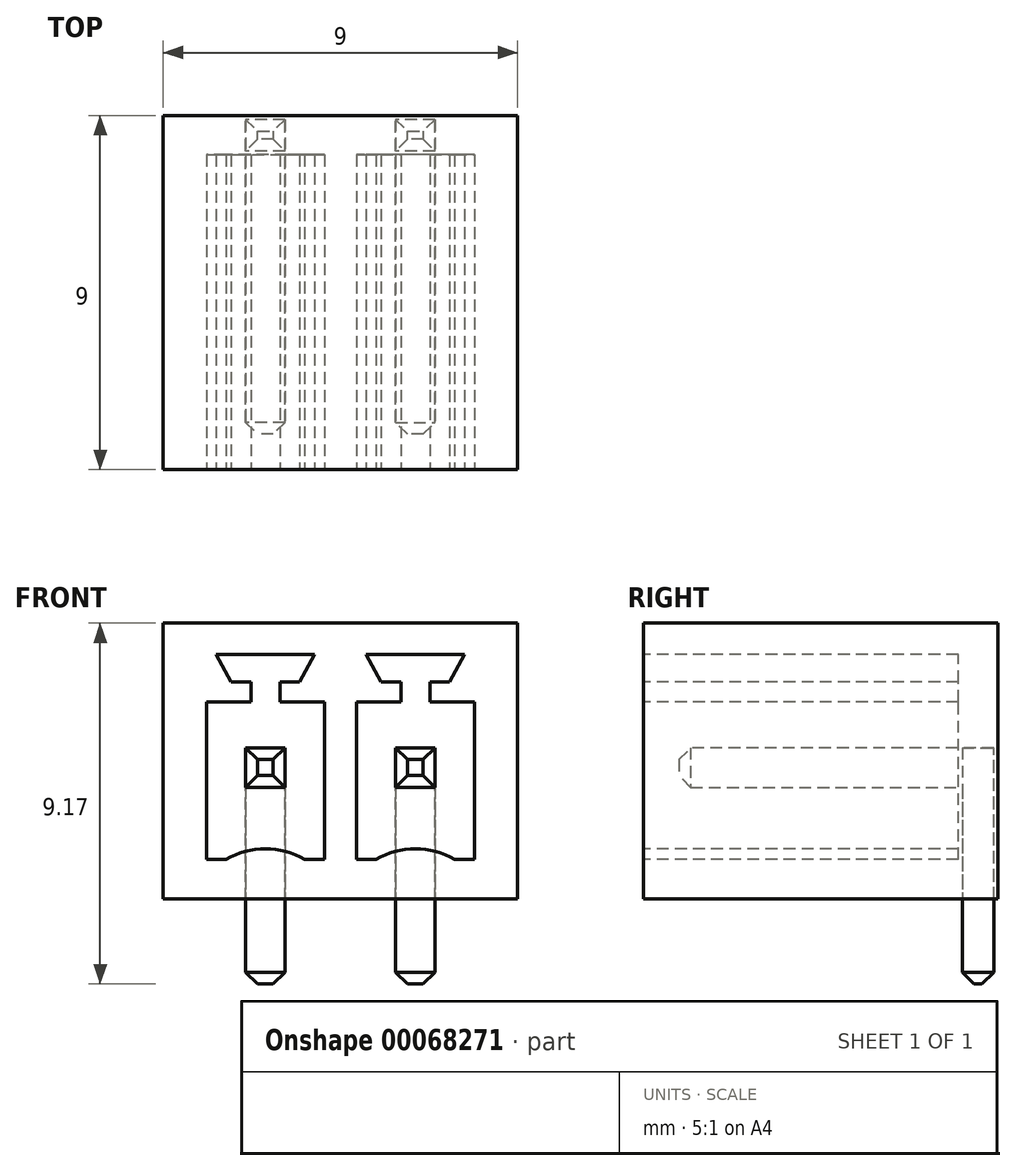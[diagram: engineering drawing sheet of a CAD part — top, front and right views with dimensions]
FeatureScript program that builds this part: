
annotation { "Feature Type Name" : "Feature", "Feature Type Description" : "" }
export const myFeature = defineFeature(function(context is Context, id is Id, definition is map)
    precondition{}
    {
        {
            var Q0;
            Q0=qCreatedBy(makeId("Top.planeOp"),FACE);
            var sketch = newSketch(context, id + "F0", { "sketchPlane" : qUnion([Q0])});
            skLineSegment(sketch, "E0.bottom", {"start": v(4.5, 4.5) * mm, "end": v(-4.5, 4.5) * mm});
            skLineSegment(sketch, "E0.top", {"start": v(4.5, -4.5) * mm, "end": v(-4.5, -4.5) * mm});
            skLineSegment(sketch, "E0.left", {"start": v(4.5, 4.5) * mm, "end": v(4.5, -4.5) * mm});
            skLineSegment(sketch, "E0.right", {"start": v(-4.5, 4.5) * mm, "end": v(-4.5, -4.5) * mm});
            skPoint(sketch, "E0.middle", {"position": v(0, 0) * mm});
            skSolve(sketch);
        }
        {
            var Q0;
            Q0=qSketchRegion(id+"F0",true);
            extrude(context, id + "F1", {"entities" : qUnion([Q0]), "depth" : 7 * mm});
        }
        {
            var Q0;
            Q0=makeQuery(id+"F1.opExtrude","SWEPT_FACE",FACE,{"disambiguationData":[OSD([sQuery(id+"F0.wireOp",EDGE,"E0.top")])]});
            var sketch = newSketch(context, id + "F2", { "sketchPlane" : qUnion([Q0])});
            skLineSegment(sketch, "E1", {"start": v(0, 0) * mm, "end": v(0, 7) * mm, "construction": true});
            skLineSegment(sketch, "E2", {"start": v(-0.4, 1) * mm, "end": v(-3.4, 1) * mm});
            skLineSegment(sketch, "E3", {"start": v(-3.4, 1) * mm, "end": v(-3.4, 5) * mm});
            skLineSegment(sketch, "E4", {"start": v(-3.4, 5) * mm, "end": v(-2.27, 5) * mm});
            skLineSegment(sketch, "E5", {"start": v(-2.27, 5) * mm, "end": v(-2.27, 5.5) * mm});
            skLineSegment(sketch, "E6", {"start": v(-2.27, 5.5) * mm, "end": v(-2.77, 5.5) * mm});
            skLineSegment(sketch, "E7", {"start": v(-2.77, 5.5) * mm, "end": v(-3.15, 6.2) * mm});
            skLineSegment(sketch, "E8", {"start": v(-3.15, 6.2) * mm, "end": v(-0.65, 6.2) * mm});
            skLineSegment(sketch, "E9", {"start": v(-0.66, 6.2) * mm, "end": v(-1.04, 5.5) * mm});
            skLineSegment(sketch, "E10", {"start": v(-1.04, 5.5) * mm, "end": v(-1.54, 5.5) * mm});
            skLineSegment(sketch, "E11", {"start": v(-1.54, 5.5) * mm, "end": v(-1.54, 5) * mm});
            skLineSegment(sketch, "E12", {"start": v(-1.54, 5) * mm, "end": v(-0.4, 5) * mm});
            skLineSegment(sketch, "E13", {"start": v(-0.4, 5) * mm, "end": v(-0.4, 1) * mm});
            skLineSegment(sketch, "E14", {"start": v(-1.9, 1) * mm, "end": v(-1.9, 6.2) * mm, "construction": true});
            skLineSegment(sketch, "E15.MirrorCS", {"start": v(0.66, 6.2) * mm, "end": v(1.04, 5.5) * mm});
            skLineSegment(sketch, "E16.MirrorCS", {"start": v(1.04, 5.5) * mm, "end": v(1.54, 5.5) * mm});
            skLineSegment(sketch, "E17.MirrorCS", {"start": v(1.54, 5.5) * mm, "end": v(1.54, 5) * mm});
            skLineSegment(sketch, "E18.MirrorCS", {"start": v(1.54, 5) * mm, "end": v(0.4, 5) * mm});
            skLineSegment(sketch, "E19.MirrorCS", {"start": v(2.27, 5) * mm, "end": v(2.27, 5.5) * mm});
            skLineSegment(sketch, "E20.MirrorCS", {"start": v(0.4, 5) * mm, "end": v(0.4, 1) * mm});
            skLineSegment(sketch, "E21.MirrorCS", {"start": v(3.4, 5) * mm, "end": v(2.27, 5) * mm});
            skLineSegment(sketch, "E22.MirrorCS", {"start": v(3.4, 1) * mm, "end": v(3.4, 5) * mm});
            skLineSegment(sketch, "E23.MirrorCS", {"start": v(0.4, 1) * mm, "end": v(3.4, 1) * mm});
            skLineSegment(sketch, "E24.MirrorCS", {"start": v(3.15, 6.2) * mm, "end": v(0.65, 6.2) * mm});
            skLineSegment(sketch, "E25.MirrorCS", {"start": v(2.27, 5.5) * mm, "end": v(2.77, 5.5) * mm});
            skLineSegment(sketch, "E26.MirrorCS", {"start": v(2.77, 5.5) * mm, "end": v(3.15, 6.2) * mm});
            skSolve(sketch);
        }
        {
            var Q0;
            Q0=qSketchRegion(id+"F2",true);
            extrude(context, id + "F3", {"entities" : qUnion([Q0]), "operationType" : NewBodyOperationType.REMOVE, "oppositeDirection" : true, "depth" : 8 * mm});
        }
        {
            var Q0;
            Q0=makeQuery(id+"F1.opExtrude","SWEPT_FACE",FACE,{"disambiguationData":[OSD([sQuery(id+"F0.wireOp",EDGE,"E0.bottom")])]});
            var sketch = newSketch(context, id + "F4", { "sketchPlane" : qUnion([Q0])});
            skLineSegment(sketch, "E27.bottom", {"start": v(-2.4, 3.84) * mm, "end": v(-1.4, 3.84) * mm});
            skLineSegment(sketch, "E27.top", {"start": v(-2.4, 0) * mm, "end": v(-1.4, 0) * mm});
            skLineSegment(sketch, "E27.left", {"start": v(-2.4, 3.84) * mm, "end": v(-2.4, 0) * mm});
            skLineSegment(sketch, "E27.right", {"start": v(-1.4, 3.84) * mm, "end": v(-1.4, 0) * mm});
            skLineSegment(sketch, "E28.bottom", {"start": v(1.4, 3.84) * mm, "end": v(2.4, 3.84) * mm});
            skLineSegment(sketch, "E28.top", {"start": v(1.4, 0) * mm, "end": v(2.4, 0) * mm});
            skLineSegment(sketch, "E28.left", {"start": v(1.4, 3.84) * mm, "end": v(1.4, 0) * mm});
            skLineSegment(sketch, "E28.right", {"start": v(2.4, 3.84) * mm, "end": v(2.4, 0) * mm});
            skPoint(sketch, "E29.centerSnap0", {"position": v(-1.9, 3.84) * mm});
            skPoint(sketch, "E30.centerSnap0", {"position": v(1.9, 3.84) * mm});
            skSolve(sketch);
        }
        {
            var Q0;
            {var subQ0=sQuery(id+"F4.wireOp",EDGE,"E27.top");Q0=makeQuery(id+"F4.imprint","IMPRINT",FACE,{"disambiguationData":[TD([[makeQuery(id+"F4.imprint","IMPRINT",EDGE,{"derivedFrom":subQ0}),1.0]])]});}
            var Q1;
            {var subQ0=sQuery(id+"F4.wireOp",EDGE,"E29");var subQ1=makeQuery(id+"F4.imprint","INTERSECT",VERTEX,{"derivedFrom":[sQuery(id+"F4.wireOp",EDGE,"E27.bottom"),subQ0]});Q1=makeQuery(id+"F4.imprint","IMPRINT",FACE,{"disambiguationData":[TD([[makeQuery(id+"F4.imprint","IMPRINT",EDGE,{"disambiguationData":[TD([[subQ1,1.0]])],"derivedFrom":subQ0}),1.0]])]});}
            var Q2;
            {var subQ0=sQuery(id+"F4.wireOp",EDGE,"E27.left");var subQ1=sQuery(id+"F4.wireOp",EDGE,"E27.bottom");var subQ2=makeQuery(id+"F4.imprint","INTERSECT",VERTEX,{"derivedFrom":[subQ1,subQ0]});Q2=makeQuery(id+"F4.imprint","IMPRINT",FACE,{"disambiguationData":[TD([[makeQuery(id+"F4.imprint","IMPRINT",EDGE,{"disambiguationData":[TD([[subQ2,-1.0]])],"derivedFrom":subQ1}),-1.0]])]});}
            var Q3;
            {var subQ0=sQuery(id+"F4.wireOp",EDGE,"E27.right");var subQ1=sQuery(id+"F4.wireOp",EDGE,"E27.bottom");var subQ2=makeQuery(id+"F4.imprint","INTERSECT",VERTEX,{"derivedFrom":[subQ1,subQ0]});Q3=makeQuery(id+"F4.imprint","IMPRINT",FACE,{"disambiguationData":[TD([[makeQuery(id+"F4.imprint","IMPRINT",EDGE,{"disambiguationData":[TD([[subQ2,1.0]])],"derivedFrom":subQ1}),-1.0]])]});}
            var Q4;
            {var subQ0=sQuery(id+"F4.wireOp",EDGE,"E28.top");Q4=makeQuery(id+"F4.imprint","IMPRINT",FACE,{"disambiguationData":[TD([[makeQuery(id+"F4.imprint","IMPRINT",EDGE,{"derivedFrom":subQ0}),1.0]])]});}
            var Q5;
            {var subQ0=sQuery(id+"F4.wireOp",EDGE,"E30");var subQ1=makeQuery(id+"F4.imprint","INTERSECT",VERTEX,{"derivedFrom":[sQuery(id+"F4.wireOp",EDGE,"E28.bottom"),subQ0]});Q5=makeQuery(id+"F4.imprint","IMPRINT",FACE,{"disambiguationData":[TD([[makeQuery(id+"F4.imprint","IMPRINT",EDGE,{"disambiguationData":[TD([[subQ1,1.0]])],"derivedFrom":subQ0}),1.0]])]});}
            var Q6;
            {var subQ0=sQuery(id+"F4.wireOp",EDGE,"E28.left");var subQ1=sQuery(id+"F4.wireOp",EDGE,"E28.bottom");var subQ2=makeQuery(id+"F4.imprint","INTERSECT",VERTEX,{"derivedFrom":[subQ1,subQ0]});Q6=makeQuery(id+"F4.imprint","IMPRINT",FACE,{"disambiguationData":[TD([[makeQuery(id+"F4.imprint","IMPRINT",EDGE,{"disambiguationData":[TD([[subQ2,-1.0]])],"derivedFrom":subQ1}),-1.0]])]});}
            var Q7;
            {var subQ0=sQuery(id+"F4.wireOp",EDGE,"E28.right");var subQ1=sQuery(id+"F4.wireOp",EDGE,"E28.bottom");var subQ2=makeQuery(id+"F4.imprint","INTERSECT",VERTEX,{"derivedFrom":[subQ1,subQ0]});Q7=makeQuery(id+"F4.imprint","IMPRINT",FACE,{"disambiguationData":[TD([[makeQuery(id+"F4.imprint","IMPRINT",EDGE,{"disambiguationData":[TD([[subQ2,1.0]])],"derivedFrom":subQ1}),-1.0]])]});}
            extrude(context, id + "F5", {"entities" : qUnion([Q0, Q1, Q2, Q3, Q4, Q5, Q6, Q7]), "operationType" : NewBodyOperationType.REMOVE, "oppositeDirection" : true, "depth" : 0.9 * mm});
        }
        {
            var Q0;
            Q0=qCreatedBy(makeId("Right.planeOp"),FACE);
            var sketch = newSketch(context, id + "F6", { "sketchPlane" : qUnion([Q0])});
            skLineSegment(sketch, "E31", {"start": v(4.4, -2.17) * mm, "end": v(4.4, 3.83) * mm});
            skLineSegment(sketch, "E32", {"start": v(4.4, 3.83) * mm, "end": v(-3.6, 3.83) * mm});
            skLineSegment(sketch, "E33", {"start": v(-3.6, 3.83) * mm, "end": v(-3.6, 2.83) * mm});
            skLineSegment(sketch, "E34", {"start": v(-3.6, 2.83) * mm, "end": v(3.6, 2.83) * mm});
            skLineSegment(sketch, "E35", {"start": v(3.6, 2.83) * mm, "end": v(3.6, -2.17) * mm});
            skLineSegment(sketch, "E36", {"start": v(3.6, -2.17) * mm, "end": v(4.4, -2.17) * mm});
            skSolve(sketch);
        }
        {
            var Q0;
            Q0=makeQuery(id+"F5.boolean.opBoolean","COPY",FACE,{"derivedFrom":makeQuery(id+"F5.opExtrude","SWEPT_FACE",FACE,{"disambiguationData":[OSD([sQuery(id+"F4.wireOp",EDGE,"E28.right")])]})});
            var sketch = newSketch(context, id + "F7", { "sketchPlane" : qUnion([Q0])});
            skLineSegment(sketch, "E37.0", {"start": v(-3.6, 3.83) * mm, "end": v(-3.6, 2.83) * mm});
            skLineSegment(sketch, "E38.0", {"start": v(4.4, 3.83) * mm, "end": v(-3.6, 3.83) * mm});
            skLineSegment(sketch, "E39.0", {"start": v(4.4, -2.17) * mm, "end": v(4.4, 3.83) * mm});
            skLineSegment(sketch, "E40.0", {"start": v(3.6, -2.17) * mm, "end": v(4.4, -2.17) * mm});
            skLineSegment(sketch, "E41.0", {"start": v(3.6, 2.83) * mm, "end": v(3.6, -2.17) * mm});
            skLineSegment(sketch, "E42.0", {"start": v(-3.6, 2.83) * mm, "end": v(3.6, 2.83) * mm});
            skSolve(sketch);
        }
        {
            var Q0;
            Q0=qSketchRegion(id+"F7",true);
            extrude(context, id + "F8", {"entities" : qUnion([Q0]), "depth" : 1 * mm});
        }
        {
            var Q0;
            Q0=makeQuery(id+"F5.boolean.opBoolean","COPY",FACE,{"derivedFrom":makeQuery(id+"F5.opExtrude","SWEPT_FACE",FACE,{"disambiguationData":[OSD([sQuery(id+"F4.wireOp",EDGE,"E27.right")])]})});
            var sketch = newSketch(context, id + "F9", { "sketchPlane" : qUnion([Q0])});
            skLineSegment(sketch, "E43.0", {"start": v(4.4, -2.17) * mm, "end": v(4.4, 3.83) * mm});
            skLineSegment(sketch, "E44.0", {"start": v(3.6, -2.17) * mm, "end": v(4.4, -2.17) * mm});
            skLineSegment(sketch, "E45.0", {"start": v(3.6, 2.83) * mm, "end": v(3.6, -2.17) * mm});
            skLineSegment(sketch, "E46.0", {"start": v(-3.6, 2.83) * mm, "end": v(3.6, 2.83) * mm});
            skLineSegment(sketch, "E47.0", {"start": v(-3.6, 3.83) * mm, "end": v(-3.6, 2.83) * mm});
            skLineSegment(sketch, "E48.0", {"start": v(4.4, 3.83) * mm, "end": v(-3.6, 3.83) * mm});
            skSolve(sketch);
        }
        {
            var Q0;
            Q0=qSketchRegion(id+"F9",true);
            extrude(context, id + "F10", {"entities" : qUnion([Q0]), "depth" : 1 * mm});
        }
        {
            var Q0;
            Q0=makeQuery(id+"F8.opExtrude","SWEPT_FACE",FACE,{"disambiguationData":[OSD([sQuery(id+"F7.wireOp",EDGE,"E37.0")])]});
            var Q1;
            Q1=makeQuery(id+"F10.opExtrude","SWEPT_FACE",FACE,{"disambiguationData":[OSD([sQuery(id+"F9.wireOp",EDGE,"E47.0")])]});
            var Q2;
            Q2=makeQuery(id+"F8.opExtrude","SWEPT_FACE",FACE,{"disambiguationData":[OSD([sQuery(id+"F7.wireOp",EDGE,"E40.0")])]});
            var Q3;
            Q3=makeQuery(id+"F10.opExtrude","SWEPT_FACE",FACE,{"disambiguationData":[OSD([sQuery(id+"F9.wireOp",EDGE,"E44.0")])]});
            chamfer(context, id + "F11", {"entities" : qUnion([Q0, Q1, Q2, Q3]), "width" : 0.3 * mm, "tangentPropagation" : true});
        }
        {
            var Q0;
            Q0=makeQuery(id+"F1.opExtrude","SWEPT_FACE",FACE,{"disambiguationData":[OSD([sQuery(id+"F0.wireOp",EDGE,"E0.top")])]});
            var sketch = newSketch(context, id + "F12", { "sketchPlane" : qUnion([Q0])});
            skArc(sketch, "E49", {"start": v(-0.9, 1) * mm, "mid": v(-1.9, 1.27) * mm, "end": v(-2.9, 1) * mm});
            skLineSegment(sketch, "E50", {"start": v(0, 7) * mm, "end": v(0, 0) * mm, "construction": true});
            skLineSegment(sketch, "E51", {"start": v(-2.9, 1) * mm, "end": v(-0.9, 1) * mm});
            skArc(sketch, "E52.MirrorCS", {"start": v(0.9, 1) * mm, "mid": v(1.9, 1.27) * mm, "end": v(2.9, 1) * mm});
            skLineSegment(sketch, "E53.MirrorCS", {"start": v(2.9, 1) * mm, "end": v(0.9, 1) * mm});
            skSolve(sketch);
        }
        {
            var Q0;
            Q0 = qSketchRegion(id + "F12", true);
            var Q1;
            Q1=makeQuery(id+"F3.boolean.opBoolean","COPY",FACE,{"derivedFrom":makeQuery(id+"F3.opExtrude","CAP_FACE",FACE,{"disambiguationData":[OSD([sQuery(id+"F2.wireOp",EDGE,"E2"),sQuery(id+"F2.wireOp",EDGE,"E3"),sQuery(id+"F2.wireOp",EDGE,"E4"),sQuery(id+"F2.wireOp",EDGE,"E5"),sQuery(id+"F2.wireOp",EDGE,"E6"),sQuery(id+"F2.wireOp",EDGE,"E7"),sQuery(id+"F2.wireOp",EDGE,"E8"),sQuery(id+"F2.wireOp",EDGE,"E9"),sQuery(id+"F2.wireOp",EDGE,"E10"),sQuery(id+"F2.wireOp",EDGE,"E11"),sQuery(id+"F2.wireOp",EDGE,"E12"),sQuery(id+"F2.wireOp",EDGE,"E13")])],"isStart":false})});
            extrude(context, id + "F13", {"entities" : qUnion([Q0]), "operationType" : NewBodyOperationType.ADD, "endBound" : BoundingType.UP_TO_SURFACE, "oppositeDirection" : true, "endBoundEntityFace" : qUnion([Q1]), "depth" : 25 * mm});
        }
    });
